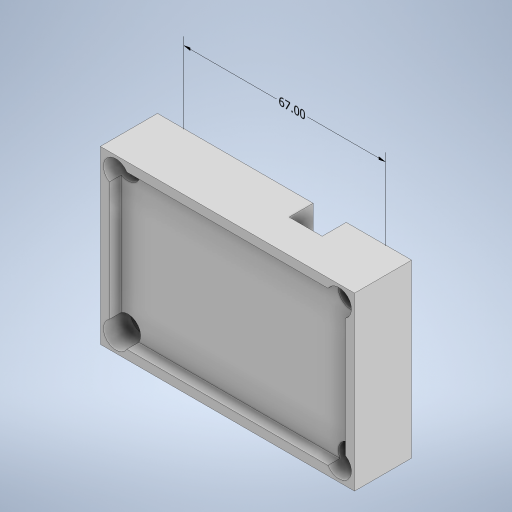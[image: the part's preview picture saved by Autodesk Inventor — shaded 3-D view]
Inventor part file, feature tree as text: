
AUTODESK INVENTOR PART (.ipt)
format: ipt  version: 2023 (Build 270158000, 158)  size: 345,088 bytes
history: native  units: mm
features: extrude x6, sketch x6, other x3
ambient origin geometry x8: Origin, YZ Plane, XZ Plane, XY Plane, X Axis, Y Axis, Z Axis, Center Point
bodies: Body1 (feature_tree)
feature tree (15):
  other  "Sólido1"
  other  "Anotaciones"
  extrude  "Extrusión1"  Depth=78.5mm
  extrude  "Extrusión2"  Depth=4.0mm TaperAngle=0.0deg
  extrude  "Extrusión3"  Depth=67.0mm
  extrude  "Extrusión4"  Depth=20.0mm
  extrude  "Extrusión5"  Depth=15.0mm TaperAngle=0.0deg
  extrude  "Extrusión6"  Depth=5.0mm TaperAngle=0.0deg
  sketch  "Boceto1"  dims[d0=51.0mm d1=78.5mm]
  sketch  "Boceto2"  dims[d2=3.0mm d3=4.0mm d4=0.0mm]
  sketch  "Boceto3"  dims[d5=15.0mm d6=0.0mm d7=67.0mm]
  sketch  "Boceto4"  dims[d8=35.0mm d9=20.0mm]
  sketch  "Boceto5"  dims[d10=8.0mm d11=0.0mm]
  sketch  "Boceto6"  dims[d12=0.0mm d13=0.0mm d14=4.5mm d15=5.0mm d16=5.0mm d17=15.0mm d18=0.0mm d19=5.0mm d20=0.0mm d21=8.4mm d22=9.0mm d23=0.0mm d24=4.5mm d25=4.5mm d26=4.5mm d28=5.0mm d29=4.5mm d30=5.0mm d31=5.0mm d32=5.0mm d33=11.0mm d34=13.0mm d38=0.0mm d35=7.42641mm d36=6.795519mm d37=67.0mm]
  other  "Cota lineal 1"
